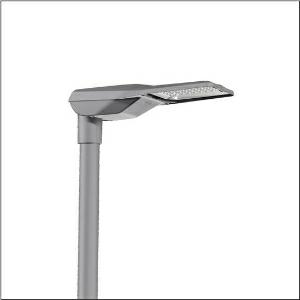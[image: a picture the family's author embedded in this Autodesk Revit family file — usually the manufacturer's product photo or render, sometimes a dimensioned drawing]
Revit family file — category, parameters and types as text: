
# Revit family: streetlight_sl_21_iq_mini___st1_0a_5xe2d61g08hb_24ab
name_source: partatom
category: Lighting Fixtures
units: mm (PartAtom-declared; Revit-internal decimal feet)

## family parameters
Cut with Voids When Loaded = No
Host = Face
Light Source = No
Part Type = Normal
Room Calculation Point = No
Round Connector Dimension = Use Diameter
Shared = No

## types (1)
- --- (1 x LED, 8480 lm, 70.9 W, 2700K)
    Apparent Load = 71 VA
    CIE Flux Codes = 37 72 97 100 100
    Color Rendering = 70
    Color Temperature = 2700K
    Default Elevation = 1800 mm
    Description = Streetlight SL 21 mini, mast luminaire, primary light control with lens, of PMMA, primary optical cover: cover, of toughened safety glass, transparent, light distribution: ST1.0a, light emission: direct distribution, primary light characteristic: asymmetric, installation type: post-top, side-entry, LED, High Power LED, rated luminous flux: 8.480lm, luminous efficacy: 120lm/W, light colour: 727, colour temperature: 2700K, control gear: ECG iQ, control: Street-Remote, Auto-Match, Temp-Guard, Lumen-Switch, Night-Set, Smart-Wire, Light-Fading, Desk-Remote (wireless, voltage-free reading and setting of iQ features in the workshop via application-optimized NFC function/RFID function), optimised constant luminous flux control (CLO 2.0), mains connection: 220..240V, AC, 50/60Hz, start of lifetime: 71W, end of lifetime: 75W, reduction: 31W, luminaire housing, of diecast aluminium, powder-coated, Siteco® metallic grey (DB 702S), corrosivity category C5 according to DIN EN ISO 12944, length: 628mm, width: 235mm, height: 110mm, spigot size: 60/76mm (post-top) and 42/60/76mm (side-entry), mast flange for spigot size: 42mm: 5XC10008XM4, 60mm: 5XC10008XM2, 76/60mm: 5XC10108XM1, protection rating (complete): IP66, insulation class (complete): insulation class II (safety insulation), certification: CE, ENEC, VDE, impact resistance: IK09, permissible operating ambient temperature for outdoor applications: -40..+50°C, standard-compliant lighting for roads and squares, packaging unit: 1 piece

Light Distribution: ST1.0a
    Height = 110 mm
    Lamp = 1 x LED
    Lamp Light Flux = 8480 lm
    Lamp Power = 70.9 W
    Lamp count = 1
    Length = 625 mm
    Luminous efficacy = 120 lm/W
    Manufacturer = Siteco
    ModVariant = No
    Model = 5XE2D61G08HB
    Number of Poles = 1
    OnlyDefault = Yes
    Power Factor = 1
    Product Name = Streetlight SL 21 iQ mini | ST1.0a
    Product group = mast luminaire | pylon top
    ProductGroupID = 6100
    Protection Class = Protection class II
    Protection Degree = IP 66
    RLX_Detail_Level = 1
    RlxData = <blob elided: 91845 chars, md5=e63a049c>
    Socket = socket
    Standby Power = 0 W
    System Light Flux = 8480 lm
    System Power = 71 W
    Type Comments = factory setting: luminous flux: 100 % | dim-lin: 254 | 711 mA
    Type Image = l_1003519.jpg
    URL = http://relux.com
    VarID = @adj_069455
    Voltage = 0 V
    Weight = 0.00 kg
    Width = 234 mm

## geometry (parser evidence)
native form markers: Blend x4, Sweep x12
no freeform markers — native parametric forms only
